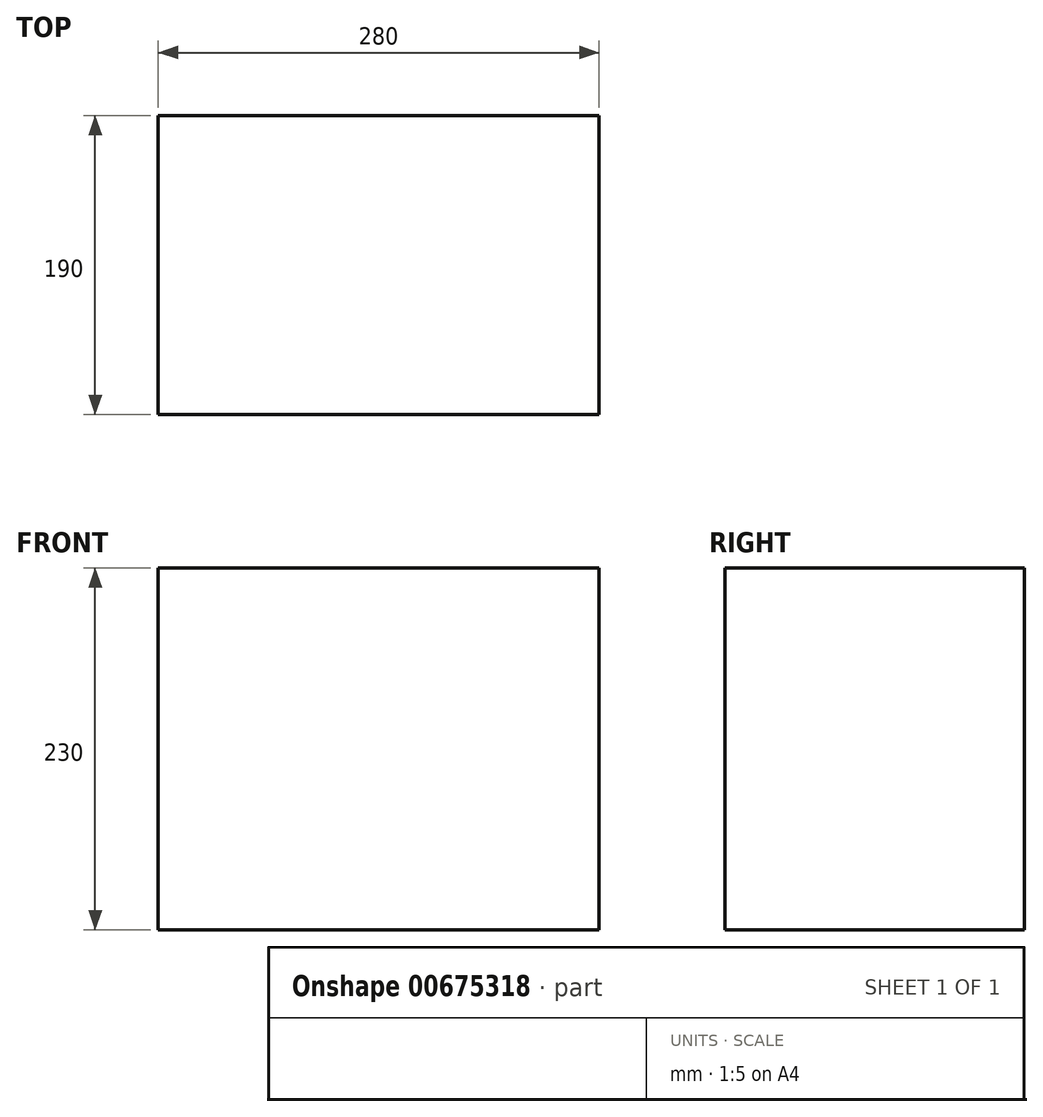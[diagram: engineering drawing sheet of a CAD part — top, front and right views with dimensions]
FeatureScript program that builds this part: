
annotation { "Feature Type Name" : "Feature", "Feature Type Description" : "" }
export const myFeature = defineFeature(function(context is Context, id is Id, definition is map)
    precondition{}
    {
        {
            var Q0;
            Q0=qCreatedBy(makeId("Top.planeOp"),FACE);
            var sketch = newSketch(context, id + "F0", { "sketchPlane" : qUnion([Q0])});
            skLineSegment(sketch, "E0.bottom", {"start": v(-141.51, 94.7) * mm, "end": v(138.49, 94.7) * mm});
            skLineSegment(sketch, "E0.top", {"start": v(-141.51, -95.3) * mm, "end": v(138.49, -95.3) * mm});
            skLineSegment(sketch, "E0.left", {"start": v(-141.51, 94.7) * mm, "end": v(-141.51, -95.3) * mm});
            skLineSegment(sketch, "E0.right", {"start": v(138.49, 94.7) * mm, "end": v(138.49, -95.3) * mm});
            skSolve(sketch);
        }
        {
            var Q0;
            Q0 = qSketchRegion(id + "F0", true);
            extrude(context, id + "F1", {"entities" : qUnion([Q0]), "depth" : 230 * mm, "offsetDistance" : 25 * mm});
        }
    });
